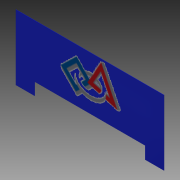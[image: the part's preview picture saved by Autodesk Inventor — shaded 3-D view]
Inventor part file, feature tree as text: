
AUTODESK INVENTOR PART (.ipt)
format: ipt  version: 2013 (Build 170138000, 138)  size: 953,344 bytes
history: native  units: in
note: dims shown in document units (in); Inventor stores cm internally (conversion verified against a paired STEP export)
features: sketch x3, other x2, extrude x1
ambient origin geometry x8: Origin, YZ Plane, XZ Plane, XY Plane, X Axis, Y Axis, Z Axis, Center Point
bodies: Solid1 (feature_tree)
feature tree (6):
  extrude  "Extrusion1"  Depth=32.0in
  sketch  "Sketch2"  dims[d2=9.25in]
  other  "Decal1"
  sketch  "Sketch1"  dims[d0=72.5in d1=32.0in]
  sketch  "Sketch3"  dims[d3=6.0in d4=9.25in d5=6.0in d6=0.125in d7=0.0in]
  other  "Image2"
